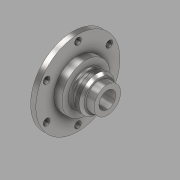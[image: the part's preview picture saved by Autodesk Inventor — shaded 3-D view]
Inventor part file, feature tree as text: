
AUTODESK INVENTOR PART (.ipt)
format: ipt  version: 2020 (Build 240168000, 168)  size: 180,224 bytes
history: native  units: mm
features: sketch x3, hole x2, other x1, revolve x1, thread x1, fillet x1
ambient origin geometry x8: Origin, YZ Plane, XZ Plane, XY Plane, X Axis, Y Axis, Z Axis, Center Point
bodies: Body1 (feature_tree)
feature tree (9):
  other  "Sólido1"
  revolve  "Revolución1"  [1 undecoded]
  hole  "Agujero1"  [1 undecoded]
  hole  "Agujero2"  [1 undecoded]
  thread  "Rosca1"  [1 undecoded]
  fillet  "Empalme1"  Radius=21.0mm
  sketch  "Boceto1"  dims[d0=50.0mm d1=6.2mm]
  sketch  "Boceto2"  dims[d2=9.6mm d3=28.5mm]
  sketch  "Boceto3"  dims[d4=6.5mm d5=3.0mm d8=18.0mm d10=21.0mm d11=60.0deg d12=18.0mm d14=9.4mm d15=135.0deg d16=9.5mm d17=41.2mm d18=15.8mm d19=90.0deg d20=20.0mm d21=6.35mm d22=44.5mm d23=9.5mm d24=90.0deg d25=8.0mm d26=20.594885mm d27=43.0mm d28=7.9mm d29=6.35mm d30=44.5mm d31=9.5mm d32=90.0deg d33=8.0mm d34=20.594885mm d35=60.0mm d37=360.0deg d39=4.668mm d40=0.0mm d41=3.0mm]
note: 4 required parameter values undecoded (feature->parameter linkage not recoverable at this tier; creation-order binding heuristic only, values carry confidence <= 0.55)